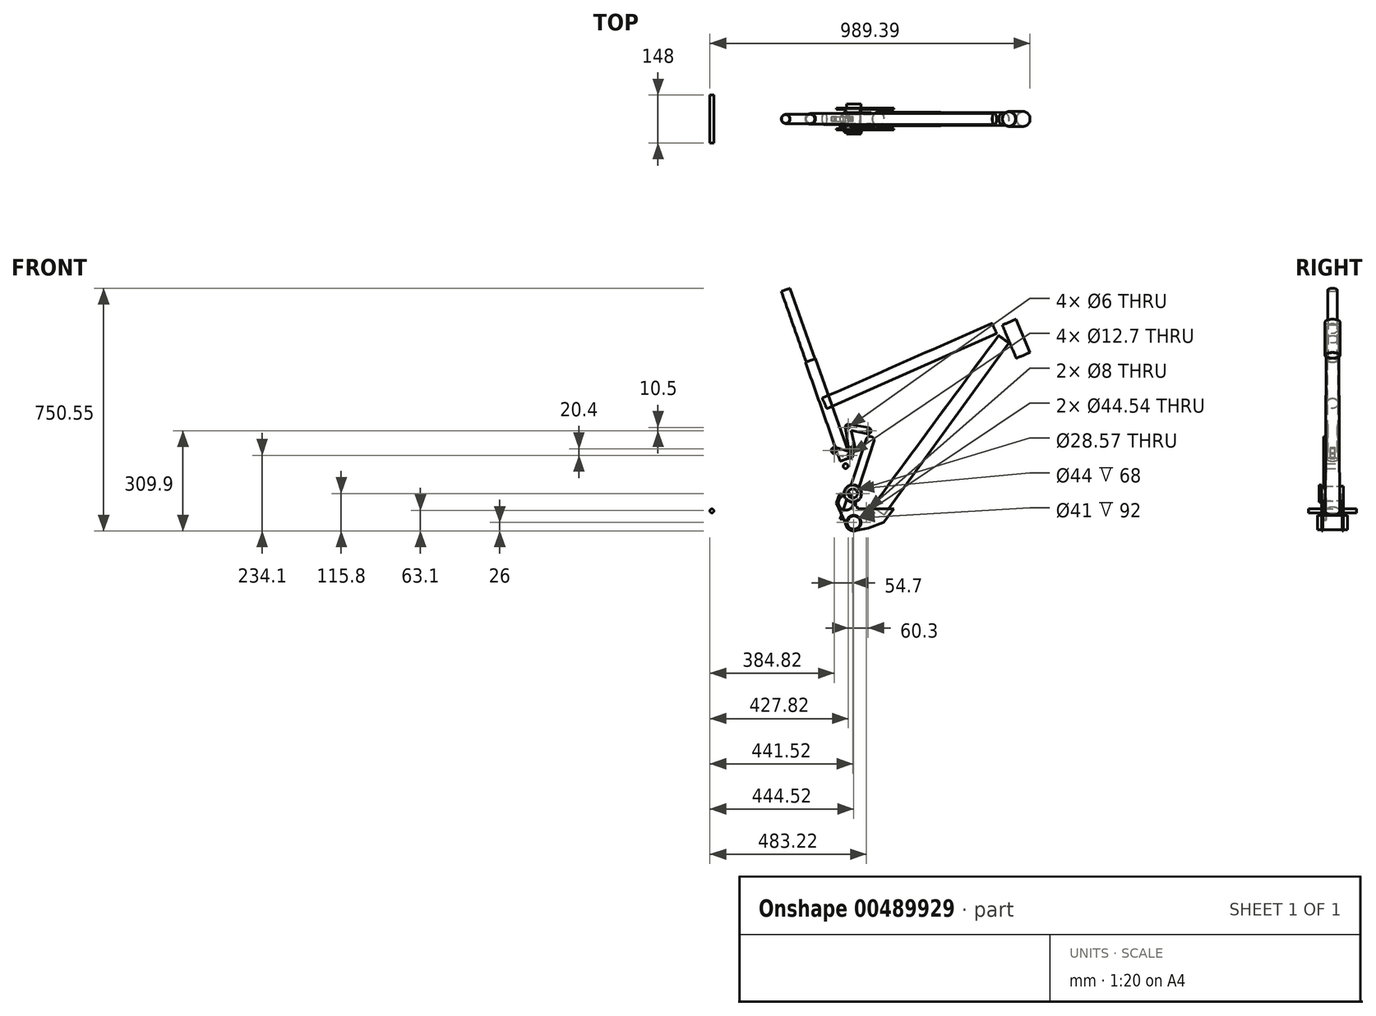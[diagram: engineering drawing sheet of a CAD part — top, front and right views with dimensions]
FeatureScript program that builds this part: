
annotation { "Feature Type Name" : "Feature", "Feature Type Description" : "" }
export const myFeature = defineFeature(function(context is Context, id is Id, definition is map)
    precondition{}
    {
        {
            var Q0;
            Q0=qCreatedBy(makeId("Front.planeOp"),FACE);
            var sketch = newSketch(context, id + "F0", { "sketchPlane" : qUnion([Q0])});
            skCircle(sketch, "E0", {"center": v(0, -36) * mm, "radius": 22.23 * mm});
            skLineSegment(sketch, "E1", {"start": v(0, -36) * mm, "end": v(523.6, 481.26) * mm});
            skLineSegment(sketch, "E2", {"start": v(523.6, 481.26) * mm, "end": v(480, 584) * mm});
            skLineSegment(sketch, "E3", {"start": v(480, 584) * mm, "end": v(-90.47, 341.85) * mm});
            skLineSegment(sketch, "E4", {"start": v(-90.47, 341.85) * mm, "end": v(-26.44, 159.42) * mm});
            skLineSegment(sketch, "E5", {"start": v(-438.52, 0) * mm, "end": v(727.9, 0) * mm, "construction": true});
            skLineSegment(sketch, "E6", {"start": v(727.9, 0) * mm, "end": v(480, 584) * mm, "construction": true});
            skLineSegment(sketch, "E7", {"start": v(480, 584) * mm, "end": v(0, 584) * mm, "construction": true});
            skLineSegment(sketch, "E8", {"start": v(-26.44, 159.42) * mm, "end": v(-210.5, 683.85) * mm});
            skLineSegment(sketch, "E9", {"start": v(0, 0) * mm, "end": v(0, -36) * mm});
            skLineSegment(sketch, "E10", {"start": v(0, -36) * mm, "end": v(-210.5, 683.85) * mm, "construction": true});
            skLineSegment(sketch, "E11", {"start": v(0, 584) * mm, "end": v(0, -36) * mm, "construction": true});
            skLineSegment(sketch, "E12", {"start": v(523.6, 481.26) * mm, "end": v(736.35, -19.93) * mm});
            skLineSegment(sketch, "E13", {"start": v(736.35, -19.93) * mm, "end": v(783.3, 0) * mm});
            skLineSegment(sketch, "E14", {"start": v(0, 0) * mm, "end": v(849.63, 0) * mm, "construction": true});
            skCircle(sketch, "E15", {"center": v(-438.52, 0) * mm, "radius": 373 * mm});
            skCircle(sketch, "E16", {"center": v(783.3, 0) * mm, "radius": 373 * mm});
            skLineSegment(sketch, "E17", {"start": v(0, -36) * mm, "end": v(0, 224.84) * mm, "construction": true});
            skSolve(sketch);
        }
        {
            var Q0;
            Q0=qCreatedBy(makeId("Front.planeOp"),FACE);
            var sketch = newSketch(context, id + "F1", { "sketchPlane" : qUnion([Q0])});
            skLineSegment(sketch, "E18", {"start": v(500.25, 592.6) * mm, "end": v(543.86, 489.86) * mm});
            skLineSegment(sketch, "E19", {"start": v(543.86, 489.86) * mm, "end": v(544.87, 490.29) * mm});
            skLineSegment(sketch, "E20", {"start": v(544.87, 490.29) * mm, "end": v(501.26, 593.04) * mm});
            skLineSegment(sketch, "E21", {"start": v(501.26, 593.04) * mm, "end": v(500.25, 592.6) * mm});
            skLineSegment(sketch, "E22", {"start": v(500.25, 592.6) * mm, "end": v(480, 584) * mm, "construction": true});
            skLineSegment(sketch, "E23", {"start": v(543.86, 489.86) * mm, "end": v(523.6, 481.26) * mm, "construction": true});
            skSolve(sketch);
        }
        {
            var Q0;
            Q0=makeQuery(id+"F1.imprint","IMPRINT",FACE,{"disambiguationData":[TD([[makeQuery(id+"F1.imprint","IMPRINT",EDGE,{"derivedFrom":sQuery(id+"F1.wireOp",EDGE,"E18")}),1.0]])]});
            var Q1;
            Q1=sQuery(id+"F0.wireOp",EDGE,"E2");
            revolve(context, id + "F2", {"entities" : qUnion([Q0]), "axis" : qUnion([Q1]), "revolveType" : RevolveType.FULL});
        }
        {
            var Q0;
            Q0=qCreatedBy(makeId("Front.planeOp"),FACE);
            var sketch = newSketch(context, id + "F3", { "sketchPlane" : qUnion([Q0])});
            skLineSegment(sketch, "E24", {"start": v(75.66, 0) * mm, "end": v(449.57, 511.85) * mm, "construction": true});
            skLineSegment(sketch, "E25", {"start": v(93.5, -12.86) * mm, "end": v(479.56, 519.36) * mm});
            skLineSegment(sketch, "E26", {"start": v(479.56, 519.36) * mm, "end": v(478.87, 519.93) * mm});
            skLineSegment(sketch, "E27", {"start": v(478.87, 519.93) * mm, "end": v(92.78, -12.33) * mm});
            skLineSegment(sketch, "E28", {"start": v(92.78, -12.33) * mm, "end": v(93.5, -12.86) * mm});
            skLineSegment(sketch, "E29", {"start": v(474.7, 471.37) * mm, "end": v(478.6, 462.16) * mm, "construction": true});
            skLineSegment(sketch, "E30", {"start": v(93.5, -12.86) * mm, "end": v(75.66, 0) * mm, "construction": true});
            skSolve(sketch);
        }
        {
            var Q0;
            Q0=makeQuery(id+"F3.imprint","IMPRINT",FACE,{"disambiguationData":[TD([[makeQuery(id+"F3.imprint","IMPRINT",EDGE,{"derivedFrom":sQuery(id+"F3.wireOp",EDGE,"E25")}),1.0]])]});
            var Q1;
            Q1=sQuery(id+"F3.wireOp",EDGE,"E24");
            revolve(context, id + "F4", {"entities" : qUnion([Q0]), "axis" : qUnion([Q1]), "revolveType" : RevolveType.FULL});
        }
        {
            var Q0;
            Q0=qCreatedBy(makeId("Front.planeOp"),FACE);
            var sketch = newSketch(context, id + "F5", { "sketchPlane" : qUnion([Q0])});
            skCircle(sketch, "E31", {"center": v(0, -36) * mm, "radius": 22.27 * mm});
            skCircle(sketch, "E32", {"center": v(0, -36) * mm, "radius": 20.5 * mm});
            skSolve(sketch);
        }
        {
            var Q0;
            Q0=makeQuery(id+"F5.imprint","IMPRINT",FACE,{"disambiguationData":[TD([[makeQuery(id+"F5.imprint","IMPRINT",EDGE,{"derivedFrom":sQuery(id+"F5.wireOp",EDGE,"E31")}),1.0]])]});
            extrude(context, id + "F6", {"entities" : qUnion([Q0]), "endBound" : BoundingType.SYMMETRIC, "depth" : 92 * mm});
        }
        {
            var Q0;
            Q0=qCreatedBy(makeId("Front.planeOp"),FACE);
            var sketch = newSketch(context, id + "F7", { "sketchPlane" : qUnion([Q0])});
            skCircle(sketch, "E33", {"center": v(-3, 53.8) * mm, "radius": 23 * mm});
            skCircle(sketch, "E34", {"center": v(-3, 53.8) * mm, "radius": 22 * mm});
            skSolve(sketch);
        }
        {
            var Q0;
            Q0=makeQuery(id+"F7.imprint","IMPRINT",FACE,{"disambiguationData":[TD([[makeQuery(id+"F7.imprint","IMPRINT",EDGE,{"derivedFrom":sQuery(id+"F7.wireOp",EDGE,"E33")}),1.0]])]});
            extrude(context, id + "F8", {"entities" : qUnion([Q0]), "endBound" : BoundingType.SYMMETRIC, "depth" : 68 * mm});
        }
        {
            var Q0;
            Q0=makeQuery(id+"F8.opExtrude","CAP_FACE",FACE,{"disambiguationData":[OSD([sQuery(id+"F7.wireOp",EDGE,"E33"),sQuery(id+"F7.wireOp",EDGE,"E34")])],"isStart":false});
            var sketch = newSketch(context, id + "F9", { "sketchPlane" : qUnion([Q0])});
            skLineSegment(sketch, "E35", {"start": v(-26, -36.5) * mm, "end": v(-54.48, 24.5) * mm});
            skCircle(sketch, "E36", {"center": v(-24.3, 25.4) * mm, "radius": 27 * mm});
            skCircle(sketch, "E37", {"center": v(0, -36) * mm, "radius": 26 * mm});
            skCircle(sketch, "E38", {"center": v(-24.3, 25.4) * mm, "radius": 23 * mm});
            skCircle(sketch, "E39", {"center": v(0, -36) * mm, "radius": 22.27 * mm});
            skLineSegment(sketch, "E40", {"start": v(11.74, -59.2) * mm, "end": v(44.87, -53.67) * mm});
            skLineSegment(sketch, "E41", {"start": v(44.87, -53.67) * mm, "end": v(91.57, -35.22) * mm});
            skLineSegment(sketch, "E42", {"start": v(91.57, -35.22) * mm, "end": v(123.48, 7.07) * mm});
            skLineSegment(sketch, "E43", {"start": v(12.46, 6.38) * mm, "end": v(0.47, 36.14) * mm});
            skLineSegment(sketch, "E44", {"start": v(0.47, 36.14) * mm, "end": v(-8.9, 53.97) * mm});
            skLineSegment(sketch, "E45", {"start": v(-54.48, 24.5) * mm, "end": v(-43.12, 52.43) * mm});
            skLineSegment(sketch, "E46", {"start": v(12.46, 6.38) * mm, "end": v(123.48, 7.07) * mm});
            skLineSegment(sketch, "E47", {"start": v(-43.12, 52.43) * mm, "end": v(-8.9, 53.97) * mm});
            skCircle(sketch, "E48", {"center": v(38.7, 1.1) * mm, "radius": 4 * mm});
            skLineSegment(sketch, "E49.bottom", {"start": v(5.24, 21.55) * mm, "end": v(50.35, 21.55) * mm});
            skLineSegment(sketch, "E49.top", {"start": v(5.24, 14.49) * mm, "end": v(50.35, 14.49) * mm});
            skLineSegment(sketch, "E49.left", {"start": v(5.24, 21.55) * mm, "end": v(5.24, 14.49) * mm});
            skLineSegment(sketch, "E49.right", {"start": v(50.35, 21.55) * mm, "end": v(50.35, 14.49) * mm});
            skSolve(sketch);
        }
        {
            var Q0;
            Q0=makeQuery(id+"F9.imprint","IMPRINT",FACE,{"disambiguationData":[TD([[makeQuery(id+"F9.imprint","IMPRINT",EDGE,{"derivedFrom":sQuery(id+"F9.wireOp",EDGE,"E38")}),-1.0]])]});
            var Q1;
            {var subQ0=sQuery(id+"F9.wireOp",EDGE,"E37");var subQ1=sQuery(id+"F9.wireOp",EDGE,"E35");var subQ2=makeQuery(id+"F9.imprint","INTERSECT",VERTEX,{"derivedFrom":[subQ1,subQ0]});Q1=makeQuery(id+"F9.imprint","IMPRINT",FACE,{"disambiguationData":[TD([[makeQuery(id+"F9.imprint","IMPRINT",EDGE,{"disambiguationData":[TD([[subQ2,-1.0]])],"derivedFrom":subQ1}),-1.0]])]});}
            var Q2;
            Q2=makeQuery(id+"F9.imprint","IMPRINT",FACE,{"disambiguationData":[TD([[makeQuery(id+"F9.imprint","IMPRINT",EDGE,{"derivedFrom":sQuery(id+"F9.wireOp",EDGE,"E39")}),-1.0]])]});
            var Q3;
            {var subQ0=sQuery(id+"F9.wireOp",EDGE,"E44");Q3=makeQuery(id+"F9.imprint","IMPRINT",FACE,{"disambiguationData":[TD([[makeQuery(id+"F9.imprint","IMPRINT",EDGE,{"derivedFrom":subQ0}),1.0]])]});}
            extrude(context, id + "F10", {"entities" : qUnion([Q0, Q1, Q2, Q3]), "oppositeDirection" : true, "depth" : 4 * mm});
        }
        {
            var Q0;
            Q0=makeQuery(id+"F9.imprint","IMPRINT",FACE,{"disambiguationData":[TD([[makeQuery(id+"F9.imprint","IMPRINT",EDGE,{"derivedFrom":sQuery(id+"F9.wireOp",EDGE,"E38")}),-1.0]])]});
            var sketch = newSketch(context, id + "F11", { "sketchPlane" : qUnion([Q0])});
            skCircle(sketch, "E50", {"center": v(-3, 53.8) * mm, "radius": 27 * mm});
            skCircle(sketch, "E51", {"center": v(-3, 53.8) * mm, "radius": 14.29 * mm});
            skSolve(sketch);
        }
        {
            var Q0;
            Q0=makeQuery(id+"F11.imprint","IMPRINT",FACE,{"disambiguationData":[TD([[makeQuery(id+"F11.imprint","IMPRINT",EDGE,{"derivedFrom":makeQuery(id+"F9.imprint","IMPRINT",EDGE,{"derivedFrom":sQuery(id+"F9.wireOp",EDGE,"E38")})}),-1.0]])]});
            var Q1;
            Q1=makeQuery(id+"F11.imprint","IMPRINT",FACE,{"disambiguationData":[TD([[makeQuery(id+"F11.imprint","IMPRINT",EDGE,{"derivedFrom":sQuery(id+"F11.wireOp",EDGE,"E51")}),-1.0]])]});
            extrude(context, id + "F12", {"entities" : qUnion([Q0, Q1]), "depth" : 7 * mm});
        }
        {
            var Q0;
            Q0=qCreatedBy(makeId("Front.planeOp"),FACE);
            var sketch = newSketch(context, id + "F13", { "sketchPlane" : qUnion([Q0])});
            skCircle(sketch, "E52", {"center": v(-438.52, 0) * mm, "radius": 6 * mm});
            skSolve(sketch);
        }
        {
            var Q0;
            Q0=makeQuery(id+"F13.imprint","IMPRINT",FACE,{"disambiguationData":[TD([[makeQuery(id+"F13.imprint","IMPRINT",EDGE,{"derivedFrom":sQuery(id+"F13.wireOp",EDGE,"E52")}),1.0]])]});
            extrude(context, id + "F14", {"entities" : qUnion([Q0]), "endBound" : BoundingType.SYMMETRIC, "depth" : 148 * mm});
        }
        {
            var Q0;
            Q0=qCreatedBy(makeId("Front.planeOp"),FACE);
            var sketch = newSketch(context, id + "F15", { "sketchPlane" : qUnion([Q0])});
            skLineSegment(sketch, "E53", {"start": v(427.71, 580.34) * mm, "end": v(-97.54, 348.94) * mm});
            skLineSegment(sketch, "E54", {"start": v(-97.54, 348.94) * mm, "end": v(-97.18, 348.12) * mm});
            skLineSegment(sketch, "E55", {"start": v(427.71, 580.34) * mm, "end": v(428.08, 579.52) * mm});
            skLineSegment(sketch, "E56", {"start": v(428.08, 579.52) * mm, "end": v(-97.18, 348.12) * mm});
            skLineSegment(sketch, "E57", {"start": v(-90.48, 332.92) * mm, "end": v(434.77, 564.33) * mm, "construction": true});
            skLineSegment(sketch, "E58", {"start": v(-90.48, 332.92) * mm, "end": v(-97.54, 348.94) * mm, "construction": true});
            skLineSegment(sketch, "E59", {"start": v(434.77, 564.33) * mm, "end": v(427.71, 580.34) * mm, "construction": true});
            skSolve(sketch);
        }
        {
            var Q0;
            Q0=qSketchRegion(id+"F15",true);
            var Q1;
            Q1=sQuery(id+"F15.wireOp",EDGE,"E57");
            revolve(context, id + "F16", {"entities" : qUnion([Q0]), "axis" : qUnion([Q1]), "revolveType" : RevolveType.FULL});
        }
        {
            var Q0;
            Q0=qCreatedBy(makeId("Front.planeOp"),FACE);
            var sketch = newSketch(context, id + "F17", { "sketchPlane" : qUnion([Q0])});
            skLineSegment(sketch, "E60", {"start": v(-26.44, 159.42) * mm, "end": v(-133.86, 465.48) * mm, "construction": true});
            skLineSegment(sketch, "E61", {"start": v(-119.13, 470.62) * mm, "end": v(-11.72, 164.59) * mm});
            skLineSegment(sketch, "E62", {"start": v(-11.72, 164.59) * mm, "end": v(-10.88, 164.88) * mm});
            skLineSegment(sketch, "E63", {"start": v(-10.88, 164.88) * mm, "end": v(-118.28, 470.91) * mm});
            skLineSegment(sketch, "E64", {"start": v(-118.28, 470.91) * mm, "end": v(-119.13, 470.62) * mm});
            skLineSegment(sketch, "E65", {"start": v(-10.88, 164.88) * mm, "end": v(-26.44, 159.42) * mm, "construction": true});
            skLineSegment(sketch, "E66", {"start": v(-133.86, 465.48) * mm, "end": v(-118.28, 470.91) * mm, "construction": true});
            skSolve(sketch);
        }
        {
            var Q0;
            Q0=makeQuery(id+"F17.imprint","IMPRINT",FACE,{"disambiguationData":[TD([[makeQuery(id+"F17.imprint","IMPRINT",EDGE,{"derivedFrom":sQuery(id+"F17.wireOp",EDGE,"E61")}),1.0]])]});
            var Q1;
            Q1=sQuery(id+"F0.wireOp",EDGE,"E8");
            revolve(context, id + "F18", {"entities" : qUnion([Q0]), "axis" : qUnion([Q1]), "revolveType" : RevolveType.FULL});
        }
        {
            var Q0;
            Q0=qCreatedBy(makeId("Front.planeOp"),FACE);
            var sketch = newSketch(context, id + "F19", { "sketchPlane" : qUnion([Q0])});
            skLineSegment(sketch, "E67", {"start": v(-210.5, 683.85) * mm, "end": v(-133.85, 465.45) * mm, "construction": true});
            skLineSegment(sketch, "E68", {"start": v(-133.85, 465.45) * mm, "end": v(-121.3, 469.85) * mm, "construction": true});
            skLineSegment(sketch, "E69", {"start": v(-121.3, 469.85) * mm, "end": v(-197.96, 688.26) * mm});
            skLineSegment(sketch, "E70", {"start": v(-197.96, 688.26) * mm, "end": v(-210.5, 683.85) * mm, "construction": true});
            skLineSegment(sketch, "E71", {"start": v(-197.11, 688.55) * mm, "end": v(-197.96, 688.26) * mm, "construction": true});
            skLineSegment(sketch, "E72", {"start": v(-197.11, 688.55) * mm, "end": v(-120.46, 470.15) * mm});
            skLineSegment(sketch, "E73", {"start": v(-121.3, 469.85) * mm, "end": v(-120.46, 470.15) * mm});
            skLineSegment(sketch, "E74", {"start": v(-197.96, 688.26) * mm, "end": v(-197.11, 688.55) * mm});
            skSolve(sketch);
        }
        {
            var Q0;
            Q0=makeQuery(id+"F19.imprint","IMPRINT",FACE,{"disambiguationData":[TD([[makeQuery(id+"F19.imprint","IMPRINT",EDGE,{"derivedFrom":sQuery(id+"F19.wireOp",EDGE,"E69")}),-1.0]])]});
            var Q1;
            Q1=sQuery(id+"F0.wireOp",EDGE,"E8");
            revolve(context, id + "F20", {"entities" : qUnion([Q0]), "axis" : qUnion([Q1]), "revolveType" : RevolveType.FULL});
        }
        {
            var Q0;
            Q0=qCreatedBy(makeId("Front.planeOp"),FACE);
            var sketch = newSketch(context, id + "F21", { "sketchPlane" : qUnion([Q0])});
            skCircle(sketch, "E75", {"center": v(-25.2, 138.7) * mm, "radius": 7.5 * mm});
            skSolve(sketch);
        }
        {
            var Q0;
            Q0=makeQuery(id+"F21.imprint","IMPRINT",FACE,{"disambiguationData":[TD([[makeQuery(id+"F21.imprint","IMPRINT",EDGE,{"derivedFrom":sQuery(id+"F21.wireOp",EDGE,"E75")}),1.0]])]});
            extrude(context, id + "F22", {"entities" : qUnion([Q0]), "endBound" : BoundingType.SYMMETRIC, "depth" : 40 * mm});
        }
        {
            var Q0;
            Q0=qCreatedBy(makeId("Front.planeOp"),FACE);
            cPlane(context, id + "F23", {"entities" : qUnion([Q0]), "cplaneType" : CPlaneType.OFFSET, "offset" : 15 * mm, "width" : 150 * mm, "height" : 150 * mm});
        }
        {
            var Q0;
            Q0=qCreatedBy(id+"F23.planeOp",FACE);
            var sketch = newSketch(context, id + "F24", { "sketchPlane" : qUnion([Q0])});
            skCircle(sketch, "E76", {"center": v(-16.7, 258.4) * mm, "radius": 3 * mm});
            skCircle(sketch, "E77", {"center": v(-25.2, 138.7) * mm, "radius": 6.35 * mm});
            skArc(sketch, "E78", {"start": v(-15.52, 268.33) * mm, "mid": v(-23.95, 265.29) * mm, "end": v(-26.56, 256.72) * mm});
            skLineSegment(sketch, "E79", {"start": v(-26.56, 256.72) * mm, "end": v(-14.22, 184.34) * mm});
            skCircle(sketch, "E80", {"center": v(43.6, 247.9) * mm, "radius": 3 * mm});
            skCircle(sketch, "E81", {"center": v(-5, 192.5) * mm, "radius": 6.35 * mm});
            skArc(sketch, "E82", {"start": v(39.77, 238.66) * mm, "mid": v(53.24, 245.22) * mm, "end": v(45.08, 257.79) * mm});
            skLineSegment(sketch, "E83", {"start": v(-15.52, 268.33) * mm, "end": v(45.08, 257.79) * mm});
            skArc(sketch, "E84", {"start": v(-14.22, 184.34) * mm, "mid": v(-3.03, 180.35) * mm, "end": v(6.32, 187.68) * mm});
            skLineSegment(sketch, "E85", {"start": v(6.32, 187.68) * mm, "end": v(-7.57, 249.15) * mm});
            skLineSegment(sketch, "E86", {"start": v(-7.57, 249.15) * mm, "end": v(39.77, 238.66) * mm});
            skSolve(sketch);
        }
        {
            var Q0;
            Q0=makeQuery(id+"F24.imprint","IMPRINT",FACE,{"disambiguationData":[TD([[makeQuery(id+"F24.imprint","IMPRINT",EDGE,{"derivedFrom":sQuery(id+"F24.wireOp",EDGE,"E76")}),-1.0]])]});
            extrude(context, id + "F25", {"entities" : qUnion([Q0]), "depth" : 4 * mm});
        }
        {
            var Q0;
            Q0=makeQuery(id+"F10.opExtrude","SWEPT_BODY",BODY,{"disambiguationData":[OSD([sQuery(id+"F9.wireOp",EDGE,"E35"),sQuery(id+"F9.wireOp",EDGE,"E36"),sQuery(id+"F9.wireOp",EDGE,"E37"),sQuery(id+"F9.wireOp",EDGE,"E38"),sQuery(id+"F9.wireOp",EDGE,"E39"),sQuery(id+"F9.wireOp",EDGE,"E40"),sQuery(id+"F9.wireOp",EDGE,"E41"),sQuery(id+"F9.wireOp",EDGE,"E42"),sQuery(id+"F9.wireOp",EDGE,"E43"),sQuery(id+"F9.wireOp",EDGE,"E45"),sQuery(id+"F9.wireOp",EDGE,"E46"),sQuery(id+"F9.wireOp",EDGE,"FK5K02xT-Tyjw-d1qf-akf6-uhemaVaazLAm"),sQuery(id+"F9.wireOp",EDGE,"mm2pKiwS-SVnP-zvIU-L5Du-A2j7p1U8S5B2"),sQuery(id+"F9.wireOp",EDGE,"IZCLW8zM-GbKn-ctCs-2ocb-lbeokmNvXhk3"),sQuery(id+"F9.wireOp",EDGE,"xYsf3Ban-L5P9-4PwF-GR1m-Uv2y4zeUiWQ5"),sQuery(id+"F9.wireOp",EDGE,"yQkTHGf5-sRyh-42L4-Ud2E-ts9FopTQnuyI"),sQuery(id+"F9.wireOp",EDGE,"t0aHAust-p0Rk-zyfR-vzEr-3oL8Lvwd0bzb"),sQuery(id+"F9.wireOp",EDGE,"Ufxdm7CI-QsJz-9KF8-LKNm-jGi75a7C4uIL"),sQuery(id+"F9.wireOp",EDGE,"ZnK2q6qZ-2Q7Z-vcdy-yBDD-ScY7AwOiJMqo"),sQuery(id+"F9.wireOp",EDGE,"Gc7Wburp-0UPy-ylzU-ry04-YMOsavYO6OQT"),sQuery(id+"F9.wireOp",EDGE,"cUvrFAy7-kfZD-SUgz-PhUw-DuEA4dqAJlpC"),sQuery(id+"F9.wireOp",EDGE,"pkUo2EjT-BdgE-IHWr-ZNv9-eBEOamu1rOXd"),sQuery(id+"F9.wireOp",EDGE,"YDDUzq19-sVF8-QGLi-mOwB-5G3ZNUy8fJTz")])]});
            var Q1;
            Q1=qCreatedBy(makeId("Front.planeOp"),FACE);
            mirror(context, id + "F26", {"entities" : qUnion([Q0]), "mirrorPlane" : qUnion([Q1])});
        }
        {
            var Q0;
            Q0=makeQuery(id+"F25.opExtrude","SWEPT_BODY",BODY,{"disambiguationData":[OSD([sQuery(id+"F24.wireOp",EDGE,"E76"),sQuery(id+"F24.wireOp",EDGE,"E77"),sQuery(id+"F24.wireOp",EDGE,"dAnCmmoZ-466u-qX6o-hDcC-m3oDPRMVMXJO"),sQuery(id+"F24.wireOp",EDGE,"aSv8fLUU-wUDJ-uzsc-UppV-udqLk2aLprjb"),sQuery(id+"F24.wireOp",EDGE,"Yv7OH4Xu-fMxE-rXm1-8sic-hcBzgtiXKYZb"),sQuery(id+"F24.wireOp",EDGE,"tyVKKrEt-jyp4-oobT-BweY-p1mvCkoPBQRs")])]});
            var Q1;
            Q1=qCreatedBy(makeId("Front.planeOp"),FACE);
            mirror(context, id + "F27", {"operationType" : NewBodyOperationType.ADD, "entities" : qUnion([Q0]), "mirrorPlane" : qUnion([Q1])});
        }
        {
            var Q0;
            Q0=makeQuery(id+"F22.opExtrude","CAP_FACE",FACE,{"disambiguationData":[OSD([sQuery(id+"F21.wireOp",EDGE,"E75")])],"isStart":false});
            cPlane(context, id + "F28", {"entities" : qUnion([Q0]), "cplaneType" : CPlaneType.OFFSET, "offset" : 0 * mm, "width" : 150 * mm, "height" : 150 * mm});
        }
        {
            var Q0;
            Q0=qCreatedBy(id+"F28.planeOp",FACE);
            var sketch = newSketch(context, id + "F29", { "sketchPlane" : qUnion([Q0])});
            skLineSegment(sketch, "E87", {"start": v(-16.43, -28.55) * mm, "end": v(-42.03, -25.46) * mm});
            skLineSegment(sketch, "E88", {"start": v(-42.03, -25.46) * mm, "end": v(38.53, 222.73) * mm});
            skLineSegment(sketch, "E89", {"start": v(63.27, 216.97) * mm, "end": v(-16.43, -28.55) * mm});
            skArc(sketch, "E90", {"start": v(63.27, 216.97) * mm, "mid": v(53.29, 230.12) * mm, "end": v(38.53, 222.73) * mm});
            skCircle(sketch, "E91", {"center": v(-3, 53.8) * mm, "radius": 23.2 * mm});
            skLineSegment(sketch, "E92", {"start": v(-16.3, 53.8) * mm, "end": v(10.3, 53.8) * mm, "construction": true});
            skSolve(sketch);
        }
        {
            var Q0;
            {var subQ0=sQuery(id+"F29.wireOp",EDGE,"E90");Q0=makeQuery(id+"F29.imprint","IMPRINT",FACE,{"disambiguationData":[TD([[makeQuery(id+"F29.imprint","IMPRINT",EDGE,{"derivedFrom":subQ0}),1.0]])]});}
            var Q1;
            {var subQ0=sQuery(id+"F29.wireOp",EDGE,"E87");Q1=makeQuery(id+"F29.imprint","IMPRINT",FACE,{"disambiguationData":[TD([[makeQuery(id+"F29.imprint","IMPRINT",EDGE,{"derivedFrom":subQ0}),-1.0]])]});}
            extrude(context, id + "F30", {"entities" : qUnion([Q0, Q1]), "depth" : 8 * mm});
        }
        {
            var Q0;
            Q0=qCreatedBy(makeId("Front.planeOp"),FACE);
            var sketch = newSketch(context, id + "F31", { "sketchPlane" : qUnion([Q0])});
            skCircle(sketch, "E93", {"center": v(-59.7, 186.9) * mm, "radius": 10 * mm});
            skCircle(sketch, "E94", {"center": v(-12.2, 172.1) * mm, "radius": 10 * mm});
            skLineSegment(sketch, "E95", {"start": v(-57.27, 196.6) * mm, "end": v(-9.23, 181.65) * mm});
            skLineSegment(sketch, "E96", {"start": v(-60.64, 176.94) * mm, "end": v(-12.76, 162.12) * mm});
            skCircle(sketch, "E97", {"center": v(-59.7, 186.9) * mm, "radius": 6.35 * mm});
            skCircle(sketch, "E98", {"center": v(-12.2, 172.1) * mm, "radius": 6.35 * mm});
            skSolve(sketch);
        }
        {
            var Q0;
            {var subQ0=sQuery(id+"F31.wireOp",EDGE,"E96");var subQ1=sQuery(id+"F31.wireOp",EDGE,"E93");var subQ2=makeQuery(id+"F31.imprint","INTERSECT",VERTEX,{"derivedFrom":[subQ1,subQ0]});Q0=makeQuery(id+"F31.imprint","IMPRINT",FACE,{"disambiguationData":[TD([[makeQuery(id+"F31.imprint","IMPRINT",EDGE,{"disambiguationData":[TD([[subQ2,-1.0]])],"derivedFrom":subQ1}),-1.0]])]});}
            var Q1;
            Q1=makeQuery(id+"F31.imprint","IMPRINT",FACE,{"disambiguationData":[TD([[makeQuery(id+"F31.imprint","IMPRINT",EDGE,{"derivedFrom":sQuery(id+"F31.wireOp",EDGE,"E97")}),-1.0]])]});
            var Q2;
            Q2=makeQuery(id+"F31.imprint","IMPRINT",FACE,{"disambiguationData":[TD([[makeQuery(id+"F31.imprint","IMPRINT",EDGE,{"derivedFrom":sQuery(id+"F31.wireOp",EDGE,"E98")}),-1.0]])]});
            extrude(context, id + "F32", {"entities" : qUnion([Q0, Q1, Q2]), "endBound" : BoundingType.SYMMETRIC, "depth" : 14 * mm});
        }
    });
